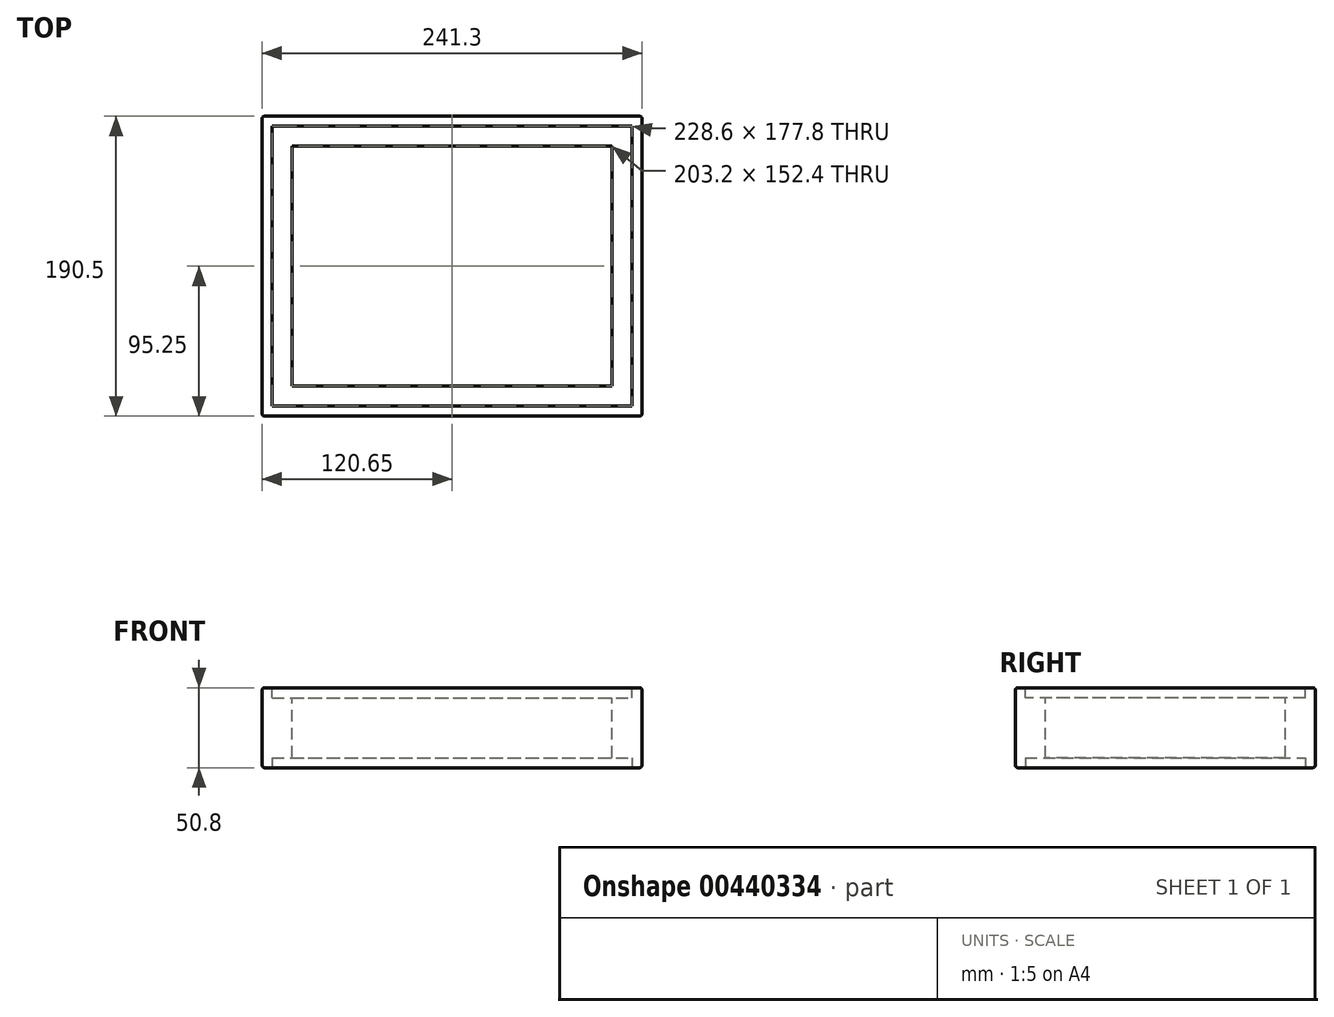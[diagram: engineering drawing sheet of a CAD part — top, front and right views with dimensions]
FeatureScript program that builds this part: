
annotation { "Feature Type Name" : "Feature", "Feature Type Description" : "" }
export const myFeature = defineFeature(function(context is Context, id is Id, definition is map)
    precondition{}
    {
        {
            var Q0;
            Q0=qCreatedBy(makeId("Front.planeOp"),FACE);
            var sketch = newSketch(context, id + "F0", { "sketchPlane" : qUnion([Q0])});
            skLineSegment(sketch, "E0.bottom", {"start": v(0, 0) * mm, "end": v(241.3, 0) * mm});
            skLineSegment(sketch, "E0.top", {"start": v(0, 50.8) * mm, "end": v(241.3, 50.8) * mm});
            skLineSegment(sketch, "E0.left", {"start": v(0, 0) * mm, "end": v(0, 50.8) * mm});
            skLineSegment(sketch, "E0.right", {"start": v(241.3, 0) * mm, "end": v(241.3, 50.8) * mm});
            skSolve(sketch);
        }
        {
            var Q0;
            Q0=makeQuery(id+"F0.imprint","IMPRINT",FACE,{"disambiguationData":[TD([[makeQuery(id+"F0.imprint","IMPRINT",EDGE,{"derivedFrom":sQuery(id+"F0.wireOp",EDGE,"E0.bottom")}),1.0]])]});
            extrude(context, id + "F1", {"entities" : qUnion([Q0]), "oppositeDirection" : true, "depth" : 190.5 * mm});
        }
        {
            var Q0;
            Q0=makeQuery(id+"F1.opExtrude","SWEPT_FACE",FACE,{"disambiguationData":[OSD([sQuery(id+"F0.wireOp",EDGE,"E0.top")])]});
            var sketch = newSketch(context, id + "F2", { "sketchPlane" : qUnion([Q0])});
            skLineSegment(sketch, "E1.bottom", {"start": v(19.05, 171.45) * mm, "end": v(222.25, 171.45) * mm});
            skLineSegment(sketch, "E1.top", {"start": v(19.05, 19.05) * mm, "end": v(222.25, 19.05) * mm});
            skLineSegment(sketch, "E1.left", {"start": v(19.05, 171.45) * mm, "end": v(19.05, 19.05) * mm});
            skLineSegment(sketch, "E1.right", {"start": v(222.25, 171.45) * mm, "end": v(222.25, 19.05) * mm});
            skSolve(sketch);
        }
        {
            var Q0;
            Q0=makeQuery(id+"F2.imprint","IMPRINT",FACE,{"disambiguationData":[TD([[makeQuery(id+"F2.imprint","IMPRINT",EDGE,{"derivedFrom":sQuery(id+"F2.wireOp",EDGE,"E1.bottom")}),-1.0]])]});
            extrude(context, id + "F3", {"entities" : qUnion([Q0]), "operationType" : NewBodyOperationType.REMOVE, "endBound" : BoundingType.UP_TO_NEXT, "oppositeDirection" : true, "depth" : 25.4 * mm});
        }
        {
            var Q0;
            Q0=makeQuery(id+"F1.opExtrude","SWEPT_FACE",FACE,{"disambiguationData":[OSD([sQuery(id+"F0.wireOp",EDGE,"E0.top")])]});
            var sketch = newSketch(context, id + "F4", { "sketchPlane" : qUnion([Q0])});
            skLineSegment(sketch, "E2.bottom", {"start": v(6.35, 184.15) * mm, "end": v(234.95, 184.15) * mm});
            skLineSegment(sketch, "E2.top", {"start": v(6.35, 6.35) * mm, "end": v(234.95, 6.35) * mm});
            skLineSegment(sketch, "E2.left", {"start": v(6.35, 184.15) * mm, "end": v(6.35, 6.35) * mm});
            skLineSegment(sketch, "E2.right", {"start": v(234.95, 184.15) * mm, "end": v(234.95, 6.35) * mm});
            skSolve(sketch);
        }
        {
            var Q0;
            Q0=makeQuery(id+"F4.imprint","IMPRINT",FACE,{"disambiguationData":[TD([[makeQuery(id+"F4.imprint","IMPRINT",EDGE,{"derivedFrom":sQuery(id+"F4.wireOp",EDGE,"E2.bottom")}),-1.0]])]});
            extrude(context, id + "F5", {"entities" : qUnion([Q0]), "operationType" : NewBodyOperationType.REMOVE, "oppositeDirection" : true, "depth" : 6.35 * mm});
        }
        {
            var Q0;
            Q0=makeQuery(id+"F1.opExtrude","SWEPT_FACE",FACE,{"disambiguationData":[OSD([sQuery(id+"F0.wireOp",EDGE,"E0.bottom")])]});
            var sketch = newSketch(context, id + "F6", { "sketchPlane" : qUnion([Q0])});
            skLineSegment(sketch, "E3.bottom", {"start": v(6.35, -6.35) * mm, "end": v(234.95, -6.35) * mm});
            skLineSegment(sketch, "E3.top", {"start": v(6.35, -184.15) * mm, "end": v(234.95, -184.15) * mm});
            skLineSegment(sketch, "E3.left", {"start": v(6.35, -6.35) * mm, "end": v(6.35, -184.15) * mm});
            skLineSegment(sketch, "E3.right", {"start": v(234.95, -6.35) * mm, "end": v(234.95, -184.15) * mm});
            skSolve(sketch);
        }
        {
            var Q0;
            Q0=makeQuery(id+"F6.imprint","IMPRINT",FACE,{"disambiguationData":[TD([[makeQuery(id+"F6.imprint","IMPRINT",EDGE,{"derivedFrom":sQuery(id+"F6.wireOp",EDGE,"E3.bottom")}),-1.0]])]});
            extrude(context, id + "F7", {"entities" : qUnion([Q0]), "operationType" : NewBodyOperationType.REMOVE, "oppositeDirection" : true, "depth" : 6.35 * mm});
        }
        {
            var Q0;
            Q0=makeQuery(id+"F1.opExtrude","CAP_EDGE",EDGE,{"disambiguationData":[OSD([sQuery(id+"F0.wireOp",EDGE,"E0.top")])],"isStart":true});
            var Q1;
            Q1=makeQuery(id+"F1.opExtrude","CAP_EDGE",EDGE,{"disambiguationData":[OSD([sQuery(id+"F0.wireOp",EDGE,"E0.left")])],"isStart":true});
            var Q2;
            Q2=makeQuery(id+"F1.opExtrude","SWEPT_EDGE",EDGE,{"disambiguationData":[OSD([sQuery(id+"F0.wireOp",EDGE,"E0.top"),sQuery(id+"F0.wireOp",EDGE,"E0.left")])]});
            var Q3;
            Q3=makeQuery(id+"F1.opExtrude","CAP_EDGE",EDGE,{"disambiguationData":[OSD([sQuery(id+"F0.wireOp",EDGE,"E0.right")])],"isStart":true});
            var Q4;
            Q4=makeQuery(id+"F1.opExtrude","SWEPT_EDGE",EDGE,{"disambiguationData":[OSD([sQuery(id+"F0.wireOp",EDGE,"E0.top"),sQuery(id+"F0.wireOp",EDGE,"E0.right")])]});
            var Q5;
            Q5=makeQuery(id+"F1.opExtrude","CAP_EDGE",EDGE,{"disambiguationData":[OSD([sQuery(id+"F0.wireOp",EDGE,"E0.top")])],"isStart":false});
            var Q6;
            Q6=makeQuery(id+"F1.opExtrude","CAP_EDGE",EDGE,{"disambiguationData":[OSD([sQuery(id+"F0.wireOp",EDGE,"E0.right")])],"isStart":false});
            var Q7;
            Q7=makeQuery(id+"F1.opExtrude","CAP_EDGE",EDGE,{"disambiguationData":[OSD([sQuery(id+"F0.wireOp",EDGE,"E0.left")])],"isStart":false});
            var Q8;
            Q8=makeQuery(id+"F1.opExtrude","CAP_EDGE",EDGE,{"disambiguationData":[OSD([sQuery(id+"F0.wireOp",EDGE,"E0.bottom")])],"isStart":false});
            var Q9;
            Q9=makeQuery(id+"F1.opExtrude","SWEPT_EDGE",EDGE,{"disambiguationData":[OSD([sQuery(id+"F0.wireOp",EDGE,"E0.bottom"),sQuery(id+"F0.wireOp",EDGE,"E0.left")])]});
            var Q10;
            Q10=makeQuery(id+"F1.opExtrude","CAP_EDGE",EDGE,{"disambiguationData":[OSD([sQuery(id+"F0.wireOp",EDGE,"E0.bottom")])],"isStart":true});
            var Q11;
            Q11=makeQuery(id+"F1.opExtrude","SWEPT_EDGE",EDGE,{"disambiguationData":[OSD([sQuery(id+"F0.wireOp",EDGE,"E0.bottom"),sQuery(id+"F0.wireOp",EDGE,"E0.right")])]});
            fillet(context, id + "F8", {"entities" : qUnion([Q0, Q1, Q2, Q3, Q4, Q5, Q6, Q7, Q8, Q9, Q10, Q11]), "radius" : 1.59 * mm, "tangentPropagation" : true, "allowEdgeOverflow" : false});
        }
    });
